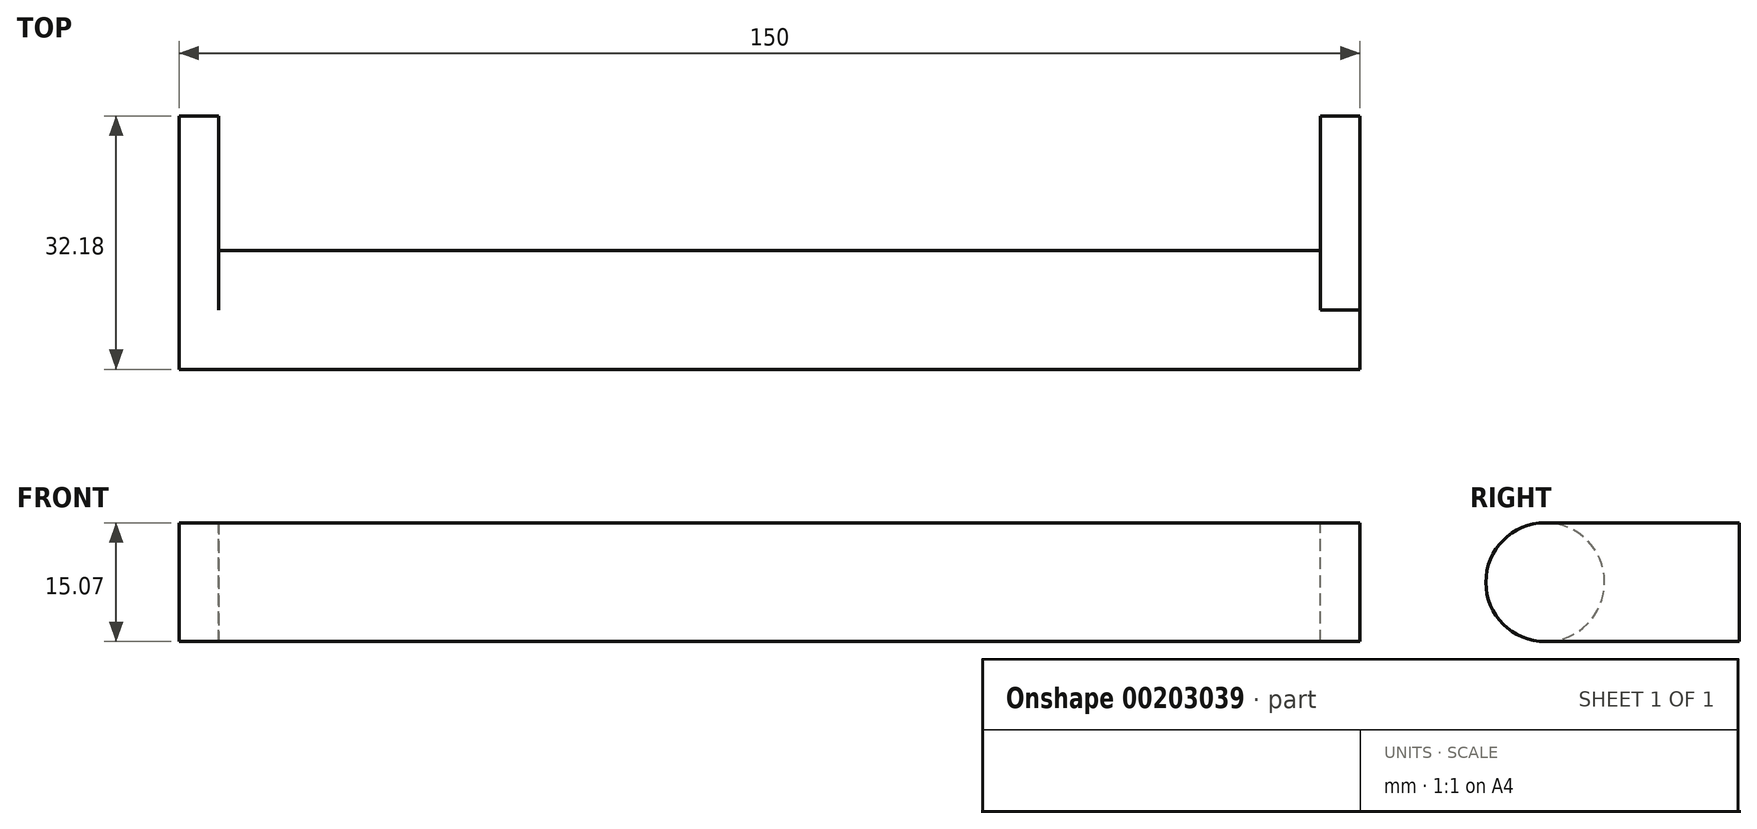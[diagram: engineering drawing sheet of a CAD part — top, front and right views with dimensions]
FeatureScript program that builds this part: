
annotation { "Feature Type Name" : "Feature", "Feature Type Description" : "" }
export const myFeature = defineFeature(function(context is Context, id is Id, definition is map)
    precondition{}
    {
        {
            var Q0;
            Q0=qCreatedBy(makeId("Front.planeOp"),FACE);
            var sketch = newSketch(context, id + "F0", { "sketchPlane" : qUnion([Q0])});
            skCircle(sketch, "E0", {"center": v(-368.43, 85.27) * mm, "radius": 7.53 * mm});
            skSolve(sketch);
        }
        {
            var Q0;
            Q0=makeQuery(id+"F0.imprint","IMPRINT",FACE,{"disambiguationData":[TD([[makeQuery(id+"F0.imprint","IMPRINT",EDGE,{"derivedFrom":sQuery(id+"F0.wireOp",EDGE,"E0")}),1.0]])]});
            extrude(context, id + "F1", {"entities" : qUnion([Q0]), "depth" : 150 * mm});
        }
        {
            var Q0;
            Q0=qCreatedBy(makeId("Front.planeOp"),FACE);
            var sketch = newSketch(context, id + "F2", { "sketchPlane" : qUnion([Q0])});
            skLineSegment(sketch, "E1.bottom", {"start": v(-368.43, 92.8) * mm, "end": v(-343.82, 92.8) * mm});
            skLineSegment(sketch, "E1.top", {"start": v(-368.43, 77.74) * mm, "end": v(-343.82, 77.74) * mm});
            skLineSegment(sketch, "E1.left", {"start": v(-368.43, 92.8) * mm, "end": v(-368.43, 77.74) * mm});
            skLineSegment(sketch, "E1.right", {"start": v(-343.82, 92.8) * mm, "end": v(-343.82, 77.74) * mm});
            skSolve(sketch);
        }
        {
            var Q0;
            Q0=makeQuery(id+"F2.imprint","IMPRINT",FACE,{"disambiguationData":[TD([[makeQuery(id+"F2.imprint","IMPRINT",EDGE,{"derivedFrom":sQuery(id+"F2.wireOp",EDGE,"E1.bottom")}),-1.0]])]});
            extrude(context, id + "F3", {"entities" : qUnion([Q0]), "operationType" : NewBodyOperationType.ADD, "depth" : 5 * mm});
        }
        {
            var Q0;
            Q0=makeQuery(id+"F1.opExtrude","CAP_FACE",FACE,{"disambiguationData":[OSD([sQuery(id+"F0.wireOp",EDGE,"E0")])],"isStart":false});
            var sketch = newSketch(context, id + "F4", { "sketchPlane" : qUnion([Q0])});
            skLineSegment(sketch, "E2.bottom", {"start": v(-368.44, 77.74) * mm, "end": v(-343.79, 77.74) * mm});
            skLineSegment(sketch, "E2.top", {"start": v(-368.44, 92.8) * mm, "end": v(-343.79, 92.8) * mm});
            skLineSegment(sketch, "E2.left", {"start": v(-368.44, 77.74) * mm, "end": v(-368.44, 92.8) * mm});
            skLineSegment(sketch, "E2.right", {"start": v(-343.79, 77.74) * mm, "end": v(-343.79, 92.8) * mm});
            skSolve(sketch);
        }
        {
            var Q0;
            {var subQ2=sQuery(id+"F4.wireOp",EDGE,"E2.top");Q0=makeQuery(id+"F4.imprint","IMPRINT",FACE,{"disambiguationData":[TD([[makeQuery(id+"F4.imprint","IMPRINT",EDGE,{"derivedFrom":subQ2}),-1.0]])]});}
            extrude(context, id + "F5", {"entities" : qUnion([Q0]), "operationType" : NewBodyOperationType.ADD, "oppositeDirection" : true, "depth" : 5 * mm});
        }
        {
            var Q0;
            Q0=makeQuery(id+"F1.opExtrude","SWEPT_BODY",BODY,{"disambiguationData":[OSD([sQuery(id+"F0.wireOp",EDGE,"E0")])]});
            var Q1;
            Q1=makeQuery(id+"F5.opExtrude","CAP_EDGE",EDGE,{"disambiguationData":[OSD([sQuery(id+"F4.wireOp",EDGE,"E2.right")])],"isStart":true});
            transform(context, id + "F6", {"entities" : qUnion([Q0]), "transformType" : TransformType.ROTATION, "transformAxis" : qUnion([Q1]), "angle" : 90 * degree, "makeCopy" : false});
        }
    });
